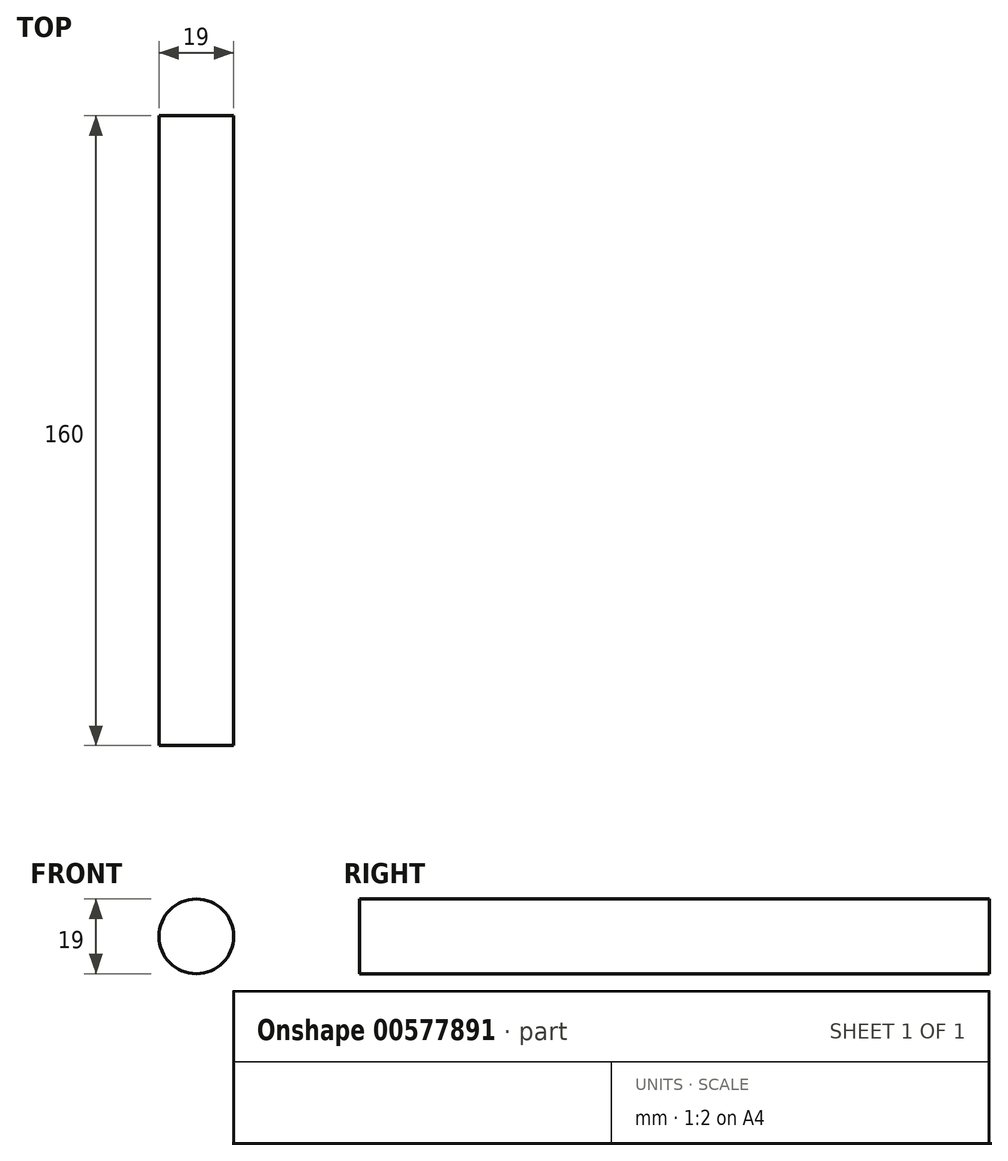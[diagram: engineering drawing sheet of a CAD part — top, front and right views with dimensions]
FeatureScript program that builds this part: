
annotation { "Feature Type Name" : "Feature", "Feature Type Description" : "" }
export const myFeature = defineFeature(function(context is Context, id is Id, definition is map)
    precondition{}
    {
        {
            var Q0;
            Q0=qCreatedBy(makeId("Front.planeOp"),FACE);
            var sketch = newSketch(context, id + "F0", { "sketchPlane" : qUnion([Q0])});
            skCircle(sketch, "E0", {"center": v(0, 0) * mm, "radius": 9.5 * mm});
            skSolve(sketch);
        }
        {
            var Q0;
            Q0 = qSketchRegion(id + "F0", true);
            extrude(context, id + "F1", {"entities" : qUnion([Q0]), "depth" : 160 * mm, "offsetDistance" : 25 * mm});
        }
    });
